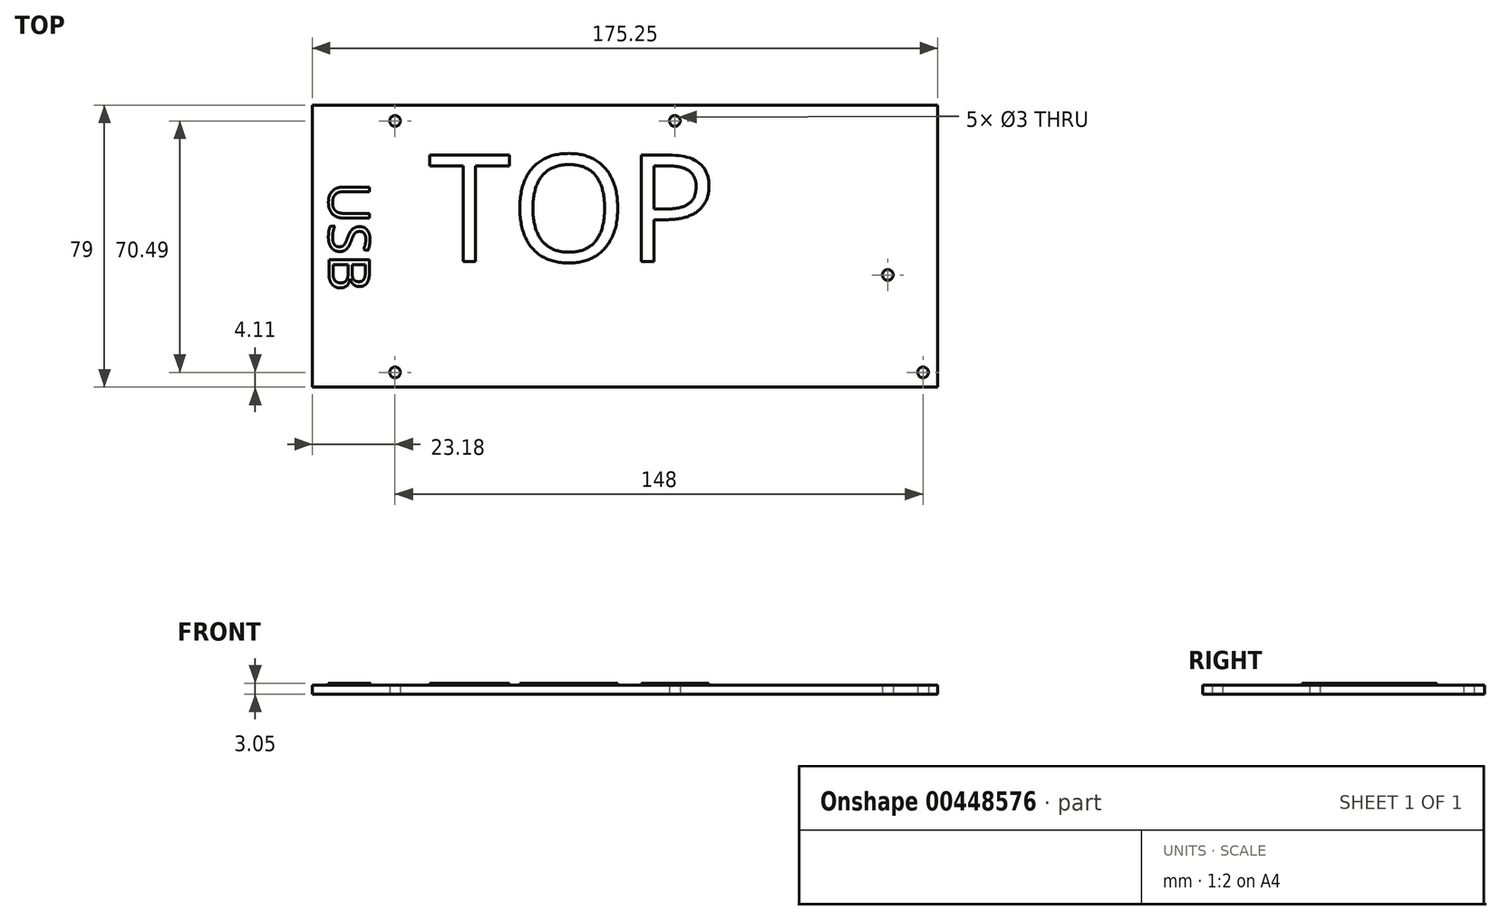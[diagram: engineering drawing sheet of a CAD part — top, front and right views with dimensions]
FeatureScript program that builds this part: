
annotation { "Feature Type Name" : "Feature", "Feature Type Description" : "" }
export const myFeature = defineFeature(function(context is Context, id is Id, definition is map)
    precondition{}
    {
        {
            var Q0;
            Q0=qCreatedBy(makeId("Top.planeOp"),FACE);
            var sketch = newSketch(context, id + "F0", { "sketchPlane" : qUnion([Q0])});
            skLineSegment(sketch, "E0.bottom", {"start": v(0, 0) * mm, "end": v(175.25, 0) * mm});
            skLineSegment(sketch, "E0.top", {"start": v(0, 79) * mm, "end": v(175.25, 79) * mm});
            skLineSegment(sketch, "E0.left", {"start": v(0, 0) * mm, "end": v(0, 79) * mm});
            skLineSegment(sketch, "E0.right", {"start": v(175.25, 0) * mm, "end": v(175.25, 79) * mm});
            skCircle(sketch, "E1", {"center": v(23.18, 74.6) * mm, "radius": 1.5 * mm});
            skLineSegment(sketch, "E2", {"start": v(23.18, 74.6) * mm, "end": v(23.18, 4.1) * mm, "construction": true});
            skLineSegment(sketch, "E3", {"start": v(23.18, 4.1) * mm, "end": v(171.18, 4.11) * mm, "construction": true});
            skCircle(sketch, "E4", {"center": v(23.18, 4.1) * mm, "radius": 1.5 * mm});
            skCircle(sketch, "E5", {"center": v(171.18, 4.11) * mm, "radius": 1.5 * mm});
            skCircle(sketch, "E6", {"center": v(101.6, 74.6) * mm, "radius": 1.5 * mm});
            skCircle(sketch, "E7", {"center": v(161.29, 31.43) * mm, "radius": 1.5 * mm});
            skSolve(sketch);
        }
        {
            var Q0;
            Q0=makeQuery(id+"F0.imprint","IMPRINT",FACE,{"disambiguationData":[TD([[makeQuery(id+"F0.imprint","IMPRINT",EDGE,{"derivedFrom":sQuery(id+"F0.wireOp",EDGE,"E0.bottom")}),1.0]])]});
            extrude(context, id + "F1", {"entities" : qUnion([Q0]), "depth" : 2.54 * mm, "offsetDistance" : 25.4 * mm});
        }
        {
            var Q0;
            Q0=makeQuery(id+"F1.opExtrude","CAP_FACE",FACE,{"disambiguationData":[OSD([sQuery(id+"F0.wireOp",EDGE,"E0.bottom"),sQuery(id+"F0.wireOp",EDGE,"E0.top"),sQuery(id+"F0.wireOp",EDGE,"E0.left"),sQuery(id+"F0.wireOp",EDGE,"E0.right"),sQuery(id+"F0.wireOp",EDGE,"E1"),sQuery(id+"F0.wireOp",EDGE,"E4"),sQuery(id+"F0.wireOp",EDGE,"E5"),sQuery(id+"F0.wireOp",EDGE,"E6"),sQuery(id+"F0.wireOp",EDGE,"E7")])],"isStart":false});
            var sketch = newSketch(context, id + "F2", { "sketchPlane" : qUnion([Q0])});
            skText(sketch, "E8", { "text": "TOP", "fontName": "OpenSans-Regular.ttf"});
            skText(sketch, "E9", { "text": "USB", "fontName": "OpenSans-Regular.ttf"});
            const initialGuessF2  = {"E8": [0.0325, 0.0352, 1, 0, 0.03008], "E9": [0.00466, 0.05753, 0, -1, 0.01145]};
            skSetInitialGuess(sketch, initialGuessF2);
            skSolve(sketch);
        }
        {
            var Q0;
            Q0 = qSketchRegion(id + "F2", true);
            extrude(context, id + "F3", {"entities" : qUnion([Q0]), "operationType" : NewBodyOperationType.ADD, "depth" : 0.5 * mm, "offsetDistance" : 25.4 * mm});
        }
    });
